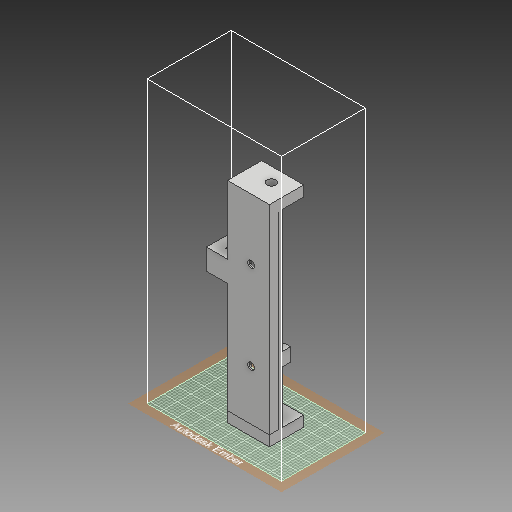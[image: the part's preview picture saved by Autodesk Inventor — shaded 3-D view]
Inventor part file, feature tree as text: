
AUTODESK INVENTOR PART (.ipt)
format: ipt  version: 2018 (Build 220112000, 112)  size: 796,672 bytes
history: native  units: mm
features: sketch x67, extrude x50, hole x8, fillet x7
ambient origin geometry x8: Origin, YZ Plane, XZ Plane, XY Plane, X Axis, Y Axis, Z Axis, Center Point
bodies: Solid1 (feature_tree)
feature tree (132):
  extrude  "Extrusion1"  Depth=100.0mm
  extrude  "Extrusion2"  Depth=5.0mm
  sketch  "Sketch3"  dims[d5=5.0mm d6=40.0mm d7=0.0mm]
  hole  "Hole1"  [1 undecoded]
  extrude  "Extrusion3"  Depth=2.0mm
  hole  "Hole2"  [1 undecoded]
  fillet  "Fillet1"  Radius=8.5mm
  extrude  "Extrusion4"  TaperAngle=90.0deg  [1 undecoded]
  extrude  "Extrusion5"  TaperAngle=180.0deg  [1 undecoded]
  hole  "Hole3"  [1 undecoded]
  fillet  "Fillet2"  Radius=3.5mm
  extrude  "Extrusion6"  Depth=10.0mm
  extrude  "Extrusion7"  Depth=5.0mm TaperAngle=0.0deg
  extrude  "Extrusion8"  Depth=5.0mm TaperAngle=0.0deg
  extrude  "Extrusion9"  Depth=0.1mm
  hole  "Hole4"  [1 undecoded]
  extrude  "Extrusion10"  Depth=5.5mm
  hole  "Hole5"  [1 undecoded]
  extrude  "Extrusion11"  Depth=2.1mm TaperAngle=0.0deg
  extrude  "Extrusion12"  Depth=5.0mm
  extrude  "Extrusion13"  Depth=1.0mm TaperAngle=0.0deg
  extrude  "Extrusion14"  Depth=3.8mm TaperAngle=0.0deg
  sketch  "Sketch21"  dims[d66=6.35mm d67=3.8mm d68=0.0mm]
  extrude  "Extrusion15"  Depth=8.0mm TaperAngle=0.0deg
  sketch  "Sketch23"  dims[d78=3.3mm d79=6.0mm d80=4.0mm d81=2.0mm d82=90.0deg d83=80.0mm d84=20.594885mm d85=5.45mm]
  extrude  "Extrusion16"  Depth=2.0mm
  extrude  "Extrusion17"  Depth=10.5mm
  hole  "Hole6"  [1 undecoded]
  fillet  "Fillet3"  Radius=4.5mm
  extrude  "Extrusion18"  Depth=8.0mm TaperAngle=0.0deg
  sketch  "Sketch28"  dims[d100=4.1mm d101=0.0mm d102=5.0mm]
  extrude  "Extrusion19"  Depth=10.0mm
  extrude  "Extrusion20"  Depth=5.0mm
  extrude  "Extrusion21"  Depth=10.0mm TaperAngle=0.0deg
  hole  "Hole7"  [1 undecoded]
  extrude  "Extrusion22"  Depth=21.0mm
  extrude  "Extrusion23"  Depth=118.0mm TaperAngle=0.0deg
  fillet  "Fillet4"  Radius=50.0mm
  fillet  "Fillet5"  Radius=7.499983mm
  extrude  "Extrusion24"  Depth=10.0mm
  extrude  "Extrusion25"  Depth=4.1mm TaperAngle=0.0deg
  hole  "Hole8"  [1 undecoded]
  extrude  "Extrusion26"  Depth=8.0mm TaperAngle=0.0deg
  sketch  "Sketch39"  dims[d142=3.85mm d143=0.0mm d144=3.0mm]
  extrude  "Extrusion27"  Depth=1.0mm
  extrude  "Extrusion28"  Depth=3.0mm
  extrude  "Extrusion29"  Depth=100.0mm TaperAngle=0.0deg
  extrude  "Extrusion30"  Depth=10.0mm
  extrude  "Extrusion31"  Depth=5.0mm
  fillet  "Fillet6"  Radius=7.5mm
  extrude  "Extrusion32"  Depth=8.0mm
  sketch  "Sketch46"  dims[d167=2.0mm d168=0.0mm d169=2.0mm d170=0.0mm]
  extrude  "Extrusion33"  Depth=5.0mm TaperAngle=0.0deg
  sketch  "Sketch48"  dims[d174=3.3mm d175=10.0mm d176=0.0mm]
  extrude  "Extrusion34"  Depth=2.0mm TaperAngle=0.0deg
  extrude  "Extrusion35"  Depth=2.0mm
  sketch  "Sketch51"  dims[d182=5.0mm d183=9.5mm d184=0.0mm]
  extrude  "Extrusion36"  Depth=10.0mm TaperAngle=0.0deg
  sketch  "Sketch53"  dims[d189=5.0mm d190=3.5mm]
  extrude  "Extrusion37"  Depth=2.0mm
  sketch  "Sketch55"  dims[d194=8.5mm d195=12.0mm]
  extrude  "Extrusion38"  Depth=5.0mm
  extrude  "Extrusion39"  Depth=9.5mm TaperAngle=0.0deg
  extrude  "Extrusion40"  Depth=9.5mm TaperAngle=0.0deg
  extrude  "Extrusion41"  Depth=5.0mm
  extrude  "Extrusion42"  Depth=9.5mm TaperAngle=0.0deg
  extrude  "Extrusion43"  Depth=12.0mm
  extrude  "Extrusion44"  Depth=12.0mm
  extrude  "Extrusion45"  Depth=3.5mm TaperAngle=0.0deg
  extrude  "Extrusion46"  Depth=3.5mm TaperAngle=0.0deg
  extrude  "Extrusion47"  Depth=3.2mm TaperAngle=0.0deg
  extrude  "Extrusion48"  Depth=3.2mm TaperAngle=0.0deg
  extrude  "Extrusion49"  Depth=101.0mm TaperAngle=0.0deg
  extrude  "Extrusion50"  Depth=4.0mm
  fillet  "Fillet7"  Radius=4.0mm
  sketch  "Sketch1"  dims[d0=22.65mm d1=100.0mm]
  sketch  "Sketch2"  dims[d2=5.0mm d3=0.0mm d4=5.0mm]
  sketch  "Sketch4"  dims[d8=10.0mm]
  sketch  "Sketch5"  dims[d9=4.0mm d10=6.0mm d11=4.0mm d12=2.0mm d13=90.0deg d14=115.0mm d15=20.594885mm d16=23.0mm]
  sketch  "Sketch6"  dims[d17=102.75mm d18=0.0mm d19=1.175mm d20=8.5mm]
  sketch  "Sketch7"  dims[d21=21.0mm d22=90.0deg]
  sketch  "Sketch8"  dims[d23=8.5mm d24=180.0deg]
  sketch  "Sketch9"  dims[d25=21.0mm]
  sketch  "Sketch10"  dims[d26=4.0mm d27=6.0mm d28=4.0mm d29=2.0mm d30=90.0deg d31=115.0mm d32=20.594885mm d33=1.0mm d34=3.5mm]
  sketch  "Sketch11"  dims[d35=15.825mm d36=10.0mm]
  sketch  "Sketch12"  dims[d37=10.0mm d38=5.0mm d39=0.0mm]
  sketch  "Sketch13"  dims[d40=5.0mm d41=12.5mm d42=0.0mm]
  sketch  "Sketch14"  dims[d43=6.0mm d44=6.0mm d45=4.0mm d46=2.0mm d47=90.0deg d48=115.0mm d49=20.594885mm d50=0.1mm]
  sketch  "Sketch15"  dims[d51=4.25mm d52=1000.0mm d53=0.0mm]
  sketch  "Sketch16"  dims[d54=3.3mm d55=5.5mm]
  sketch  "Sketch17"  dims[d56=3.2mm d57=3.0mm]
  sketch  "Sketch18"  dims[d58=2.1mm d59=91.25mm d60=0.0mm]
  sketch  "Sketch19"  dims[d61=4.44mm d62=5.0mm]
  sketch  "Sketch20"  dims[d63=1.0mm d64=91.25mm d65=0.0mm]
  sketch  "Sketch22"  dims[d69=3.3mm d70=6.0mm d71=4.0mm d72=2.0mm d73=90.0deg d74=8.0mm d75=20.594885mm d76=4.55mm d77=0.0mm]
  sketch  "Sketch24"  dims[d86=129.8mm d87=0.0mm d88=10.5mm]
  sketch  "Sketch25"  dims[d89=2.5mm d90=0.0mm d91=10.0mm d92=4.5mm d93=0.0mm]
  sketch  "Sketch26"  dims[d94=8.0mm d95=0.0mm d96=15.5mm d97=0.0mm]
  sketch  "Sketch27"  dims[d98=10.0mm d99=10.0mm]
  sketch  "Sketch29"  dims[d103=17.5mm d104=10.0mm d105=0.0mm]
  sketch  "Sketch30"  dims[d106=5.0mm]
  sketch  "Sketch31"  dims[d107=6.0mm d108=6.0mm d109=4.0mm d110=2.0mm d111=90.0deg d112=80.0mm d113=20.594885mm d114=2.0mm]
  sketch  "Sketch32"  dims[d115=45.0mm d116=0.0mm d117=21.0mm]
  sketch  "Sketch33"  dims[d118=4.5mm d119=118.0mm d120=0.0mm d121=50.0mm d122=7.499983mm]
  sketch  "Sketch34"  dims[d123=7.5mm d124=10.0mm]
  sketch  "Sketch35"  dims[d125=10.0mm d126=4.1mm d127=0.0mm]
  sketch  "Sketch36"  dims[d128=13.4mm d129=0.0mm d130=5.0mm]
  sketch  "Sketch37"  dims[d131=6.0mm d132=6.0mm d133=4.0mm d134=2.0mm d135=90.0deg d136=8.0mm d137=20.594885mm d138=130.4mm d139=0.0mm]
  sketch  "Sketch38"  dims[d140=1.0mm d141=1.0mm]
  sketch  "Sketch40"  dims[d145=2.0mm d146=100.0mm d147=0.0mm]
  sketch  "Sketch41"  dims[d148=4.0mm d149=10.0mm]
  sketch  "Sketch42"  dims[d150=5.0mm d151=15.0mm d152=7.5mm]
  sketch  "Sketch43"  dims[d153=7.5mm d154=0.0mm]
  sketch  "Sketch44"  dims[d155=6.0mm d156=6.0mm d157=4.0mm d158=2.0mm d159=90.0deg d160=8.0mm d161=20.594885mm d162=5.5mm]
  sketch  "Sketch45"  dims[d163=5.0mm d164=0.0mm d165=5.5mm d166=0.0mm]
  sketch  "Sketch47"  dims[d171=2.0mm d172=0.0mm d173=20.0mm]
  sketch  "Sketch49"  dims[d177=2.0mm d178=3.5mm]
  sketch  "Sketch50"  dims[d179=5.0mm d180=0.0mm d181=8.5mm]
  sketch  "Sketch52"  dims[d185=9.5mm d186=0.0mm d187=2.7mm d188=0.0mm]
  sketch  "Sketch54"  dims[d191=7.5mm d192=9.5mm d193=0.0mm]
  sketch  "Sketch56"  dims[d196=10.25mm d197=0.0mm d198=12.0mm]
  sketch  "Sketch57"  dims[d199=10.25mm d200=0.0mm d201=3.5mm d202=0.0mm]
  sketch  "Sketch58"  dims[d203=3.75mm d204=3.5mm d205=0.0mm]
  sketch  "Sketch59"  dims[d206=9.6mm d207=3.2mm d208=0.0mm]
  sketch  "Sketch60"  dims[d209=9.6mm d210=3.2mm d211=0.0mm]
  sketch  "Sketch61"  dims[d212=5.5mm d213=101.0mm d214=0.0mm]
  sketch  "Sketch62"  dims[d215=3.5mm d216=0.0mm d217=4.0mm d218=4.0mm d219=0.0mm]
  sketch  "Sketch63"  dims[d220=9.7mm]
  sketch  "Sketch64"  dims[d221=106.25mm d222=0.0mm]
  sketch  "Sketch65"  dims[d223=9.8mm]
  sketch  "Sketch66"  dims[d224=1.8mm d225=0.0mm]
  sketch  "Sketch67"  dims[d226=9.8mm d227=1.8mm d228=0.0mm d229=5.0mm d230=180.0mm d231=0.0mm d232=2.875mm d233=2.875mm d234=3.0mm d235=3.0mm d236=5.0mm d237=0.0mm d238=1.0mm]
note: 10 required parameter values undecoded (feature->parameter linkage not recoverable at this tier; creation-order binding heuristic only, values carry confidence <= 0.55)
